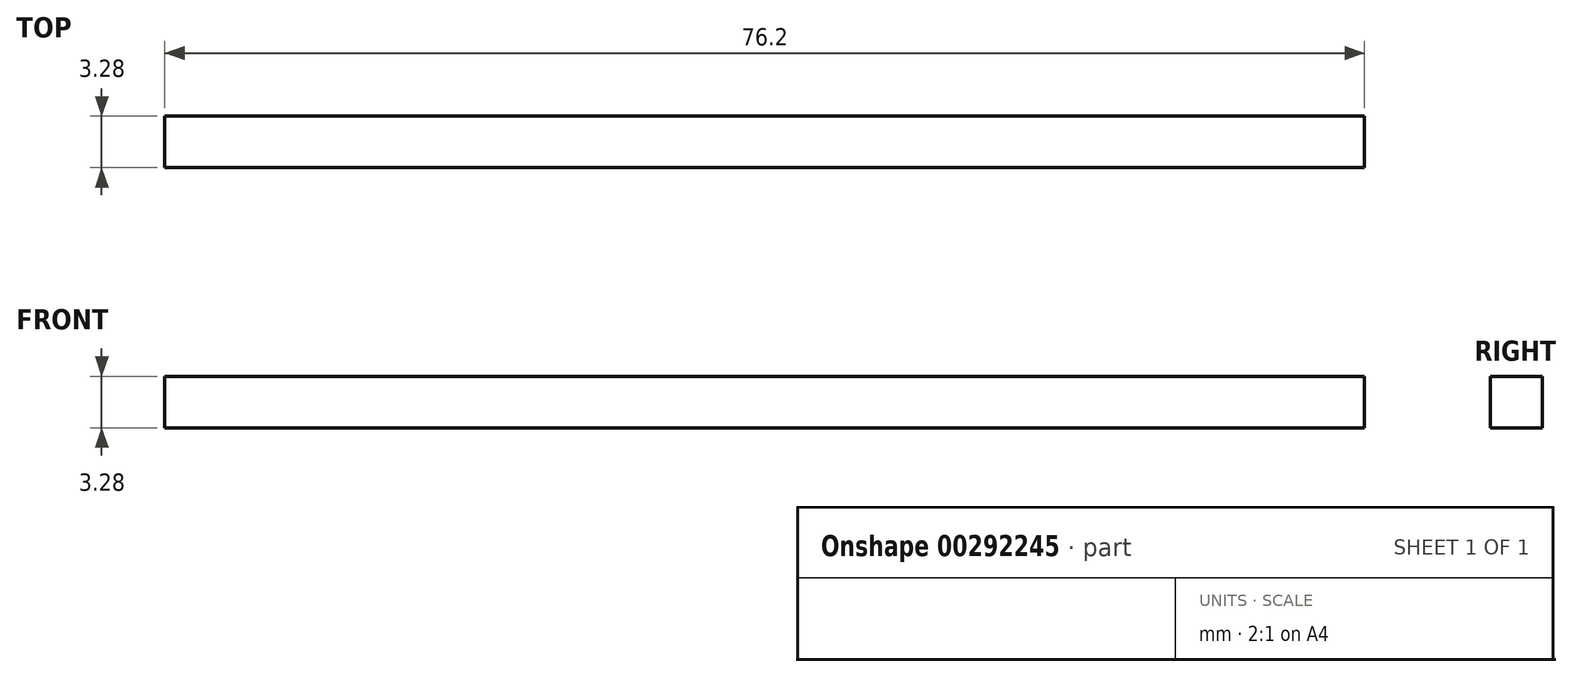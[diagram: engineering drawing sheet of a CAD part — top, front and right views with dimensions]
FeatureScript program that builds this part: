
annotation { "Feature Type Name" : "Feature", "Feature Type Description" : "" }
export const myFeature = defineFeature(function(context is Context, id is Id, definition is map)
    precondition{}
    {
        {
            var Q0;
            Q0=qCreatedBy(makeId("Right.planeOp"),FACE);
            var sketch = newSketch(context, id + "F0", { "sketchPlane" : qUnion([Q0])});
            skLineSegment(sketch, "E0.bottom", {"start": v(1.64, -1.64) * mm, "end": v(-1.64, -1.64) * mm});
            skLineSegment(sketch, "E0.top", {"start": v(1.64, 1.64) * mm, "end": v(-1.64, 1.64) * mm});
            skLineSegment(sketch, "E0.left", {"start": v(1.64, -1.64) * mm, "end": v(1.64, 1.64) * mm});
            skLineSegment(sketch, "E0.right", {"start": v(-1.64, -1.64) * mm, "end": v(-1.64, 1.64) * mm});
            skPoint(sketch, "E0.middle", {"position": v(0, 0) * mm});
            skSolve(sketch);
        }
        {
            var Q0;
            Q0 = qSketchRegion(id + "F0", true);
            extrude(context, id + "F1", {"entities" : qUnion([Q0]), "depth" : 76.2 * mm});
        }
    });
